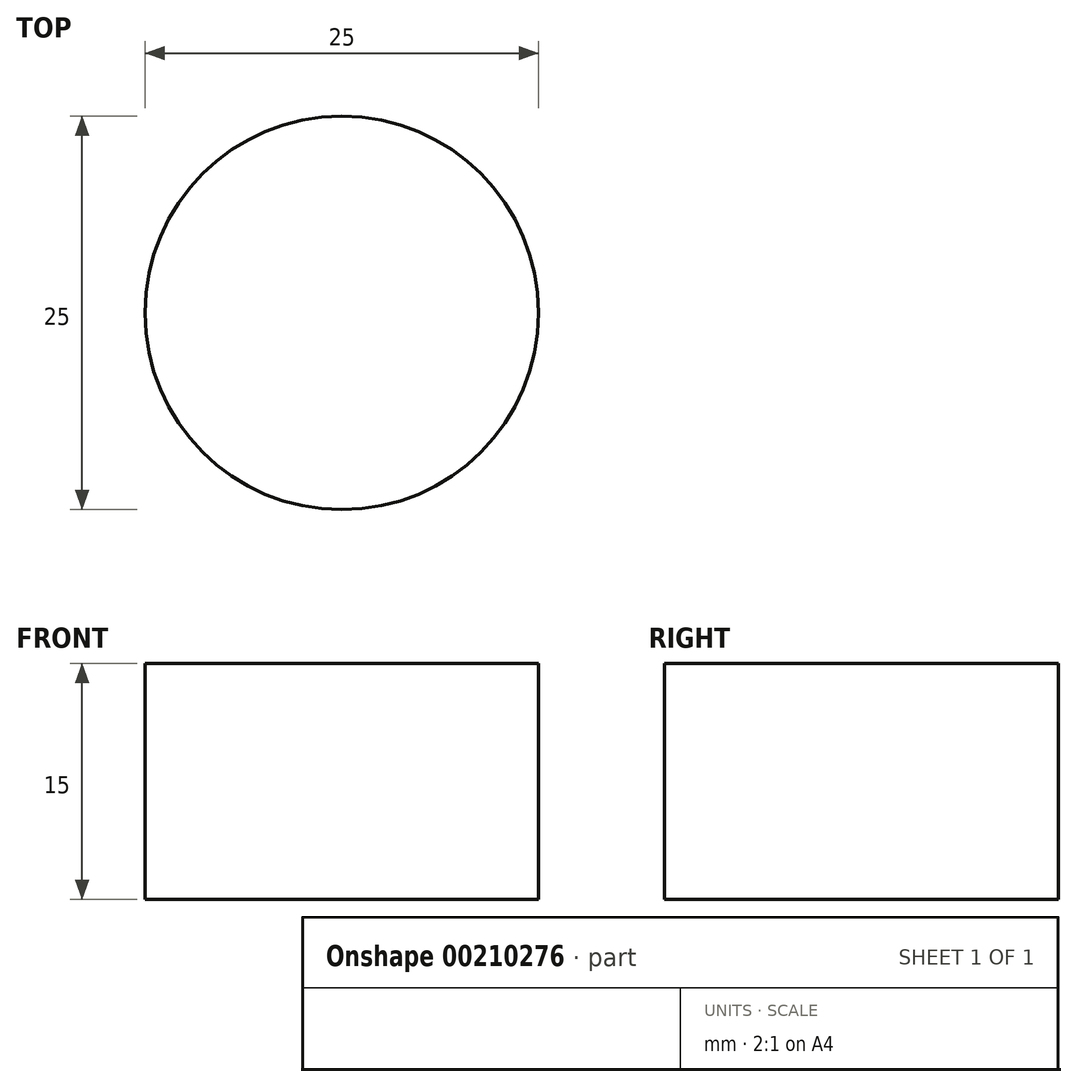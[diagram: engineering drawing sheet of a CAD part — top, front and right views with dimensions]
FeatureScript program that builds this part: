
annotation { "Feature Type Name" : "Feature", "Feature Type Description" : "" }
export const myFeature = defineFeature(function(context is Context, id is Id, definition is map)
    precondition{}
    {
        {
            var Q0;
            Q0=qCreatedBy(makeId("Top.planeOp"),FACE);
            var sketch = newSketch(context, id + "F0", { "sketchPlane" : qUnion([Q0])});
            skCircle(sketch, "E0", {"center": v(0, 0) * mm, "radius": 12.5 * mm});
            skSolve(sketch);
        }
        {
            var Q0;
            Q0=qSketchRegion(id+"F0",true);
            extrude(context, id + "F1", {"entities" : qUnion([Q0]), "depth" : 15 * mm});
        }
    });
